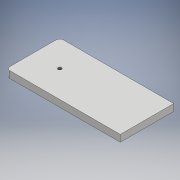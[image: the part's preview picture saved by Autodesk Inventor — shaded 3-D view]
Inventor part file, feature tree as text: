
AUTODESK INVENTOR PART (.ipt)
format: ipt  version: 2018 (Build 220112000, 112)  size: 109,056 bytes
history: native  units: mm
features: other x6, sketch x2, extrude x1, hole x1, fillet x1
ambient origin geometry x8: Origin, YZ Plane, XZ Plane, XY Plane, X Axis, Y Axis, Z Axis, Center Point
bodies: Body1 (feature_tree)
feature tree (11):
  other  "Sólido1"
  extrude  "Extrusão1"  Depth=160.0mm
  hole  "Furo2"  [1 undecoded]
  fillet  "Arredondamento3"  Radius=6.0mm
  sketch  "Esboço1"  dims[d0=160.0mm d1=160.0mm]
  other  "Referência1"
  other  "Referência2"
  sketch  "Esboço11"  dims[d2=75.0mm d3=9.52mm d4=0.0mm d95=6.0mm d96=4.917mm d97=12.0mm d98=4.0mm d99=2.0mm d100=90.0deg d101=17.1mm d102=20.594885mm d103=5.0mm]
  other  "<userpath>\Documents\OpenCNC\MONTAGEM\CNC1.iam"
  other  "CNC1.iam"
  other  "PERFIL_ESTRUTURAL_40X80_EIXO_Y:1"
note: 1 required parameter value undecoded (feature->parameter linkage not recoverable at this tier; creation-order binding heuristic only, values carry confidence <= 0.55)
